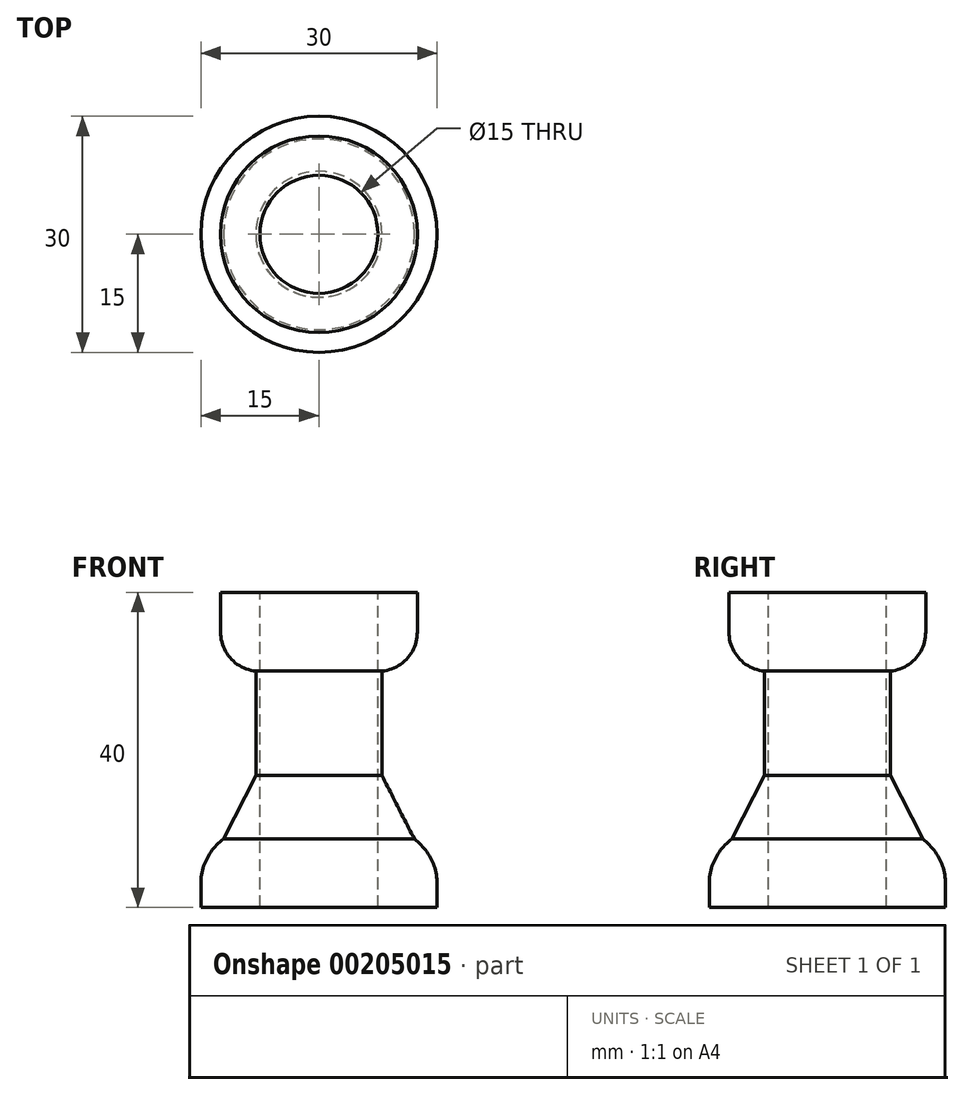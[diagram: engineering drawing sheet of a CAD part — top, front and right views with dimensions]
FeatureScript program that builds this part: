
annotation { "Feature Type Name" : "Feature", "Feature Type Description" : "" }
export const myFeature = defineFeature(function(context is Context, id is Id, definition is map)
    precondition{}
    {
        {
            var Q0;
            Q0=qCreatedBy(makeId("Top.planeOp"),FACE);
            var sketch = newSketch(context, id + "F0", { "sketchPlane" : qUnion([Q0])});
            skCircle(sketch, "E0", {"center": v(0, 0) * mm, "radius": 15 * mm});
            skSolve(sketch);
        }
        {
            var Q0;
            Q0=makeQuery(id+"F0.imprint","IMPRINT",FACE,{"disambiguationData":[TD([[makeQuery(id+"F0.imprint","IMPRINT",EDGE,{"derivedFrom":sQuery(id+"F0.wireOp",EDGE,"E0")}),1.0]])]});
            extrude(context, id + "F1", {"entities" : qUnion([Q0]), "depth" : 10 * mm});
        }
        {
            var Q0;
            Q0=makeQuery(id+"F1.opExtrude","CAP_EDGE",EDGE,{"disambiguationData":[OSD([sQuery(id+"F0.wireOp",EDGE,"E0")])],"isStart":false});
            fillet(context, id + "F2", {"entities" : qUnion([Q0]), "radius" : 7 * mm, "tangentPropagation" : true, "allowEdgeOverflow" : false});
        }
        {
            var Q0;
            Q0=makeQuery(id+"F1.opExtrude","CAP_FACE",FACE,{"disambiguationData":[OSD([sQuery(id+"F0.wireOp",EDGE,"E0")])],"isStart":false});
            extrude(context, id + "F3", {"entities" : qUnion([Q0]), "operationType" : NewBodyOperationType.ADD, "depth" : 20 * mm});
        }
        {
            var Q0;
            {var subQ0=sQuery(id+"F0.wireOp",EDGE,"E0");Q0=makeQuery(id+"F3.boolean.opBoolean","MERGE",EDGE,{"derivedFrom":[makeQuery(id+"F2.opFillet","BLEND_EDGE",EDGE,{"blendedFrom":[makeQuery(id+"F1.opExtrude","CAP_EDGE",EDGE,{"disambiguationData":[OSD([subQ0])],"isStart":false}),makeQuery(id+"F1.opExtrude","CAP_FACE",FACE,{"disambiguationData":[OSD([subQ0])],"isStart":false})],"blendedInto":[makeQuery(id+"F1.opExtrude","CAP_FACE",FACE,{"disambiguationData":[OSD([subQ0])],"isStart":false})]}),makeQuery(id+"F3.opExtrude","CAP_EDGE",EDGE,{"disambiguationData":[OSD([subQ0])],"isStart":true})]});}
            chamfer(context, id + "F4", {"entities" : qUnion([Q0]), "width" : 10 * mm, "tangentPropagation" : true});
        }
        {
            var Q0;
            Q0=makeQuery(id+"F3.opExtrude","CAP_FACE",FACE,{"disambiguationData":[OSD([sQuery(id+"F0.wireOp",EDGE,"E0")])],"isStart":false});
            var sketch = newSketch(context, id + "F5", { "sketchPlane" : qUnion([Q0])});
            skCircle(sketch, "E1", {"center": v(0, 0) * mm, "radius": 12.5 * mm});
            skSolve(sketch);
        }
        {
            var Q0;
            Q0=makeQuery(id+"F5.imprint","IMPRINT",FACE,{"disambiguationData":[TD([[makeQuery(id+"F5.imprint","IMPRINT",EDGE,{"derivedFrom":makeQuery(id+"F3.opExtrude","CAP_EDGE",EDGE,{"disambiguationData":[OSD([sQuery(id+"F0.wireOp",EDGE,"E0")])],"isStart":false})}),1.0]])]});
            var Q1;
            Q1=makeQuery(id+"F5.imprint","IMPRINT",FACE,{"disambiguationData":[TD([[makeQuery(id+"F5.imprint","IMPRINT",EDGE,{"derivedFrom":sQuery(id+"F5.wireOp",EDGE,"E1")}),1.0]])]});
            extrude(context, id + "F6", {"entities" : qUnion([Q0, Q1]), "operationType" : NewBodyOperationType.ADD, "depth" : 10 * mm});
        }
        {
            var Q0;
            Q0=makeQuery(id+"F6.opExtrude","CAP_EDGE",EDGE,{"disambiguationData":[OSD([sQuery(id+"F5.wireOp",EDGE,"E1")])],"isStart":true});
            fillet(context, id + "F7", {"entities" : qUnion([Q0]), "radius" : 5 * mm, "tangentPropagation" : true, "allowEdgeOverflow" : false});
        }
        {
            var Q0;
            Q0=makeQuery(id+"F6.opExtrude","CAP_FACE",FACE,{"disambiguationData":[OSD([sQuery(id+"F5.wireOp",EDGE,"E1")])],"isStart":false});
            var sketch = newSketch(context, id + "F8", { "sketchPlane" : qUnion([Q0])});
            skCircle(sketch, "E2", {"center": v(0, 0) * mm, "radius": 7.5 * mm});
            skSolve(sketch);
        }
        {
            var Q0;
            Q0=sQuery(id+"F8.wireOp",VERTEX,"E2.center");
            var Q1;
            Q1=makeQuery(id+"F1.opExtrude","SWEPT_BODY",BODY,{"disambiguationData":[OSD([sQuery(id+"F0.wireOp",EDGE,"E0")])]});
            hole(context, id + "F9", {"style" : HoleStyle.SIMPLE, "endStyle" : HoleEndStyle.THROUGH, "holeDiameter" : 15 * mm, "startFromSketch" : true, "locations" : qUnion([Q0]), "scope" : qUnion([Q1]), "isTappedThrough" : true});
        }
    });
